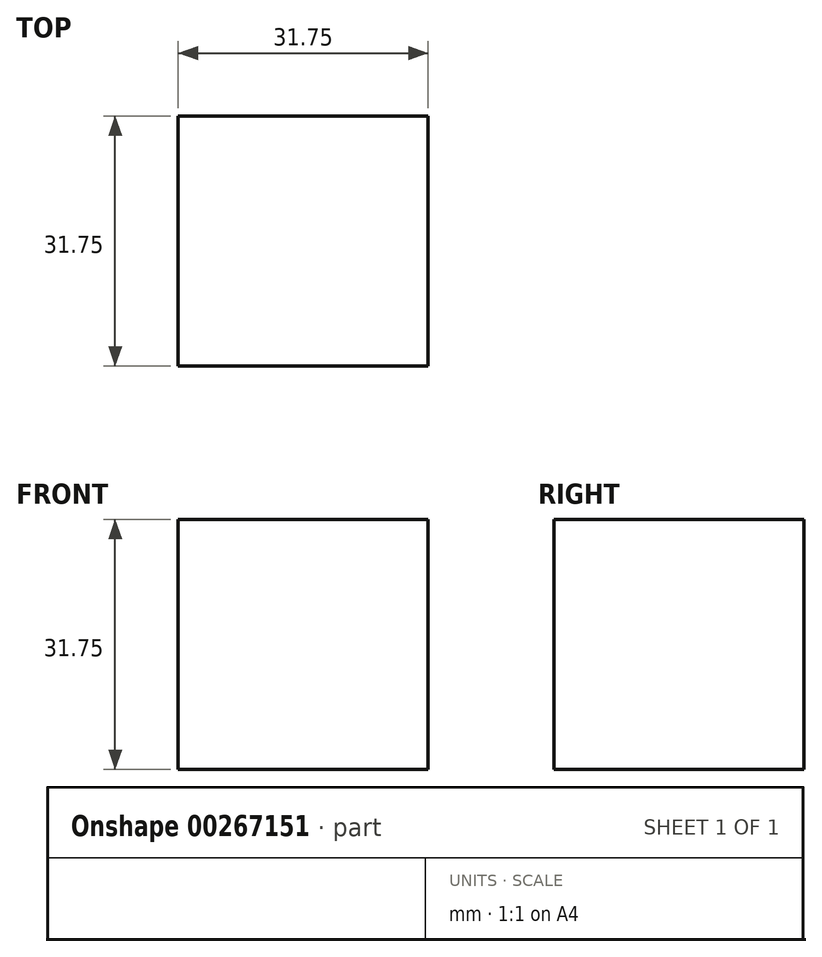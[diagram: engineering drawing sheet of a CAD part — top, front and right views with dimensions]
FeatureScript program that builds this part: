
annotation { "Feature Type Name" : "Feature", "Feature Type Description" : "" }
export const myFeature = defineFeature(function(context is Context, id is Id, definition is map)
    precondition{}
    {
        {
            var Q0;
            Q0=qCreatedBy(makeId("Top.planeOp"),FACE);
            var sketch = newSketch(context, id + "F0", { "sketchPlane" : qUnion([Q0])});
            skLineSegment(sketch, "E0.bottom", {"start": v(0, -37.03) * mm, "end": v(31.75, -37.03) * mm});
            skLineSegment(sketch, "E0.top", {"start": v(0, -5.28) * mm, "end": v(31.75, -5.28) * mm});
            skLineSegment(sketch, "E0.left", {"start": v(0, -37.03) * mm, "end": v(0, -5.28) * mm});
            skLineSegment(sketch, "E0.right", {"start": v(31.75, -37.03) * mm, "end": v(31.75, -5.28) * mm});
            skSolve(sketch);
        }
        {
            var Q0;
            Q0=makeQuery(id+"F0.imprint","IMPRINT",FACE,{"disambiguationData":[TD([[makeQuery(id+"F0.imprint","IMPRINT",EDGE,{"derivedFrom":sQuery(id+"F0.wireOp",EDGE,"E0.bottom")}),1.0]])]});
            extrude(context, id + "F1", {"entities" : qUnion([Q0]), "depth" : 31.75 * mm});
        }
    });
